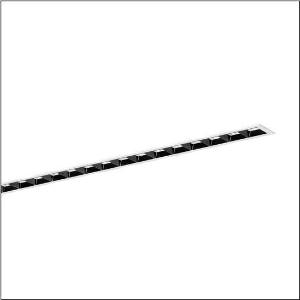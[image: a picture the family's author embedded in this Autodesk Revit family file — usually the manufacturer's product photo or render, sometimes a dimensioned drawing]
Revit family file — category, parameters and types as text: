
# Revit family: silica_r__21_51mx11tctaw_2435
name_source: partatom
category: Lighting Fixtures
units: mm (PartAtom-declared; Revit-internal decimal feet)

## family parameters
Cut with Voids When Loaded = No
Host = Face
Light Source = No
Part Type = Normal
Room Calculation Point = No
Round Connector Dimension = Use Diameter
Shared = No

## types (1)
- --- (1 x LED, 9300 lm, 80.5 W, 6500K)
    Apparent Load = 81 VA
    CIE Flux Codes = 85 99 100 100 100
    Color Rendering = 80
    Color Temperature = 6500K
    Default Elevation = 1800 mm
    Description = Silica® 21, office luminaire, primary light control with darklight reflector, of PMMA, black, CAT 2 (L<= 3000cd/m²), light emission: direct distribution, primary light characteristic: symmetric, installation type: recessed, LED, rated luminous flux: 9.300lm, luminous efficacy: 110lm/W, light colour: 8tw, colour temperature: 2700..6500K, with terminal, 3+2-pole, max. 2.5mm², mains connection: 220..240V, AC, 50/60Hz, rated input power: 84.6W, luminaire housing, of aluminium, traffic white (RAL 9016), length: 3.028mm, width: 79mm, height: 53mm, protection rating (complete): IP20, insulation class (complete): insulation class I (protective earthing), certification: CE, permissible operating ambient temperature: 0..+35°C, standard: EN 50419, packaging unit: 1 piece
    Height = 0 mm  [stored 0 ft]
    Lamp = 1 x LED
    Lamp Light Flux = 9300 lm
    Lamp Power = 80.5 W
    Lamp count = 1
    Length = 3027 mm
    Luminous efficacy = 116 lm/W
    Manufacturer = Siteco
    ModVariant = No
    Model = 51MX11TCTAW
    Mounting Place = Ceiling
    Mounting Type = Recessed
    Number of Poles = 1
    OnlyDefault = Yes
    Power Factor = 1
    Product Name = Silica® 21
    Product group = office luminaire | ceiling recessed
    ProductGroupID = 401
    Protection Class = Protection class I
    Protection Degree = IP 20
    RLX_Detail_Level = 1
    RLX_Emergency_Light_Flux = 0 lm
    RLX_Emergency_Type = 0
    RLX_Emergency_Type_DB = No
    RlxData = <blob elided: 60069 chars, md5=63740a05>
    Socket = socket
    Standby Power = 0 W
    System Light Flux = 9300 lm
    System Power = 81 W
    Type Comments = individual setting
    Type Image = l_1297791.jpg
    URL = http://relux.com
    VarID = @adj_071419
    Voltage = 0 V
    Weight = 0.00 kg
    Width = 79 mm

note: [stored X ft] marks values corroborated as IEEE doubles in the binary element streams (Revit-internal decimal feet)

## geometry (parser evidence)
native form markers: Blend x4, Sweep x11
no freeform markers — native parametric forms only
